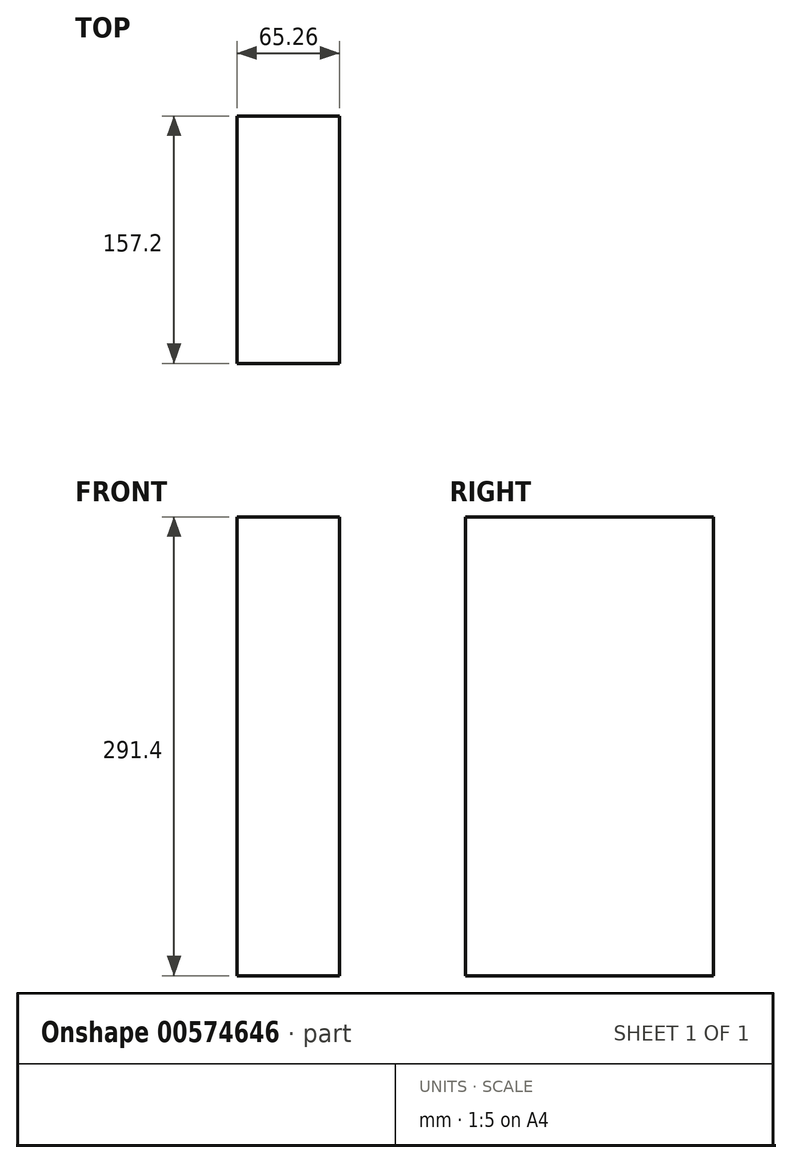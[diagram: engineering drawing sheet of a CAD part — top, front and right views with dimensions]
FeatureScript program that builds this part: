
annotation { "Feature Type Name" : "Feature", "Feature Type Description" : "" }
export const myFeature = defineFeature(function(context is Context, id is Id, definition is map)
    precondition{}
    {
        {
            var Q0;
            Q0=qCreatedBy(makeId("Top.planeOp"),FACE);
            var sketch = newSketch(context, id + "F0", { "sketchPlane" : qUnion([Q0])});
            skLineSegment(sketch, "E0.bottom", {"start": v(-133.04, 191.9) * mm, "end": v(-67.78, 191.9) * mm});
            skLineSegment(sketch, "E0.top", {"start": v(-133.04, 34.7) * mm, "end": v(-67.78, 34.7) * mm});
            skLineSegment(sketch, "E0.left", {"start": v(-133.04, 191.9) * mm, "end": v(-133.04, 34.7) * mm});
            skLineSegment(sketch, "E0.right", {"start": v(-67.78, 191.9) * mm, "end": v(-67.78, 34.7) * mm});
            skSolve(sketch);
        }
        {
            var Q0;
            Q0 = qSketchRegion(id + "F0", true);
            extrude(context, id + "F1", {"entities" : qUnion([Q0]), "depth" : 291.4 * mm, "offsetDistance" : 25.4 * mm});
        }
    });
